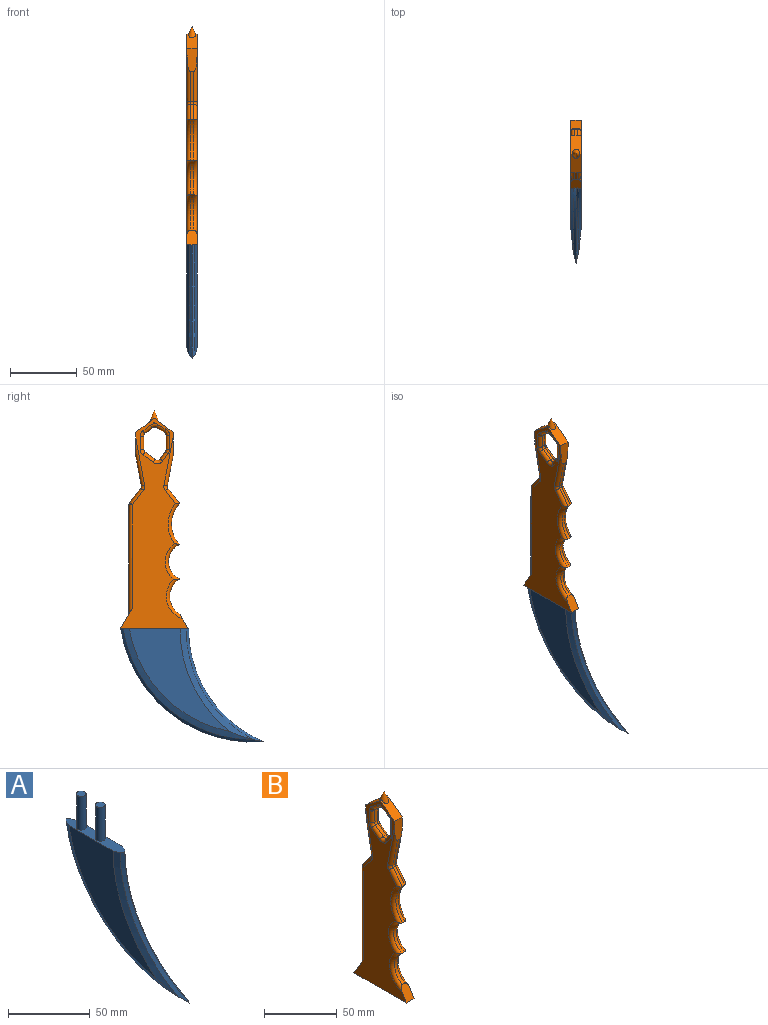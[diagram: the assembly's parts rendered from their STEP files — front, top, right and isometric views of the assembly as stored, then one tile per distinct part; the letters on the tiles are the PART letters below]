
ASSEMBLY  parts=2 mates=1
PART A: 15 faces, bbox 7.6x107.1x112.1 mm
  f0: plane 50.82x7.64mm, normal (0,0,1), area 295.1mm2, adj f1,f2,f3,f4,f5,f6,f7,f8
  f1: plane 76.85x75.17mm, normal (1,0,0), area 2128.3mm2, adj f0,f9,f10
  f2: plane 76.85x75.17mm, normal (-1,0,0), area 2128.3mm2, adj f0,f7,f8
  f3: cone r=100.59mm half-angle=45deg, axis (1,0,0), area 410.6mm2, adj f0,f4,f5,f7
  f4: cone r=96.78mm half-angle=45deg, axis (-1,0,0), area 410.6mm2, adj f0,f3,f6,f9
  f5: cone r=95.52mm half-angle=45deg, axis (-1,0,0), area 298.2mm2, adj f0,f3,f6,f8
  f6: cone r=91.71mm half-angle=45deg, axis (1,0,0), area 298.2mm2, adj f0,f4,f5,f10
  f7: cone r=94.24mm half-angle=67.5deg, axis (1,0,0), area 593mm2, adj f0,f2,f3,f8
  f8: cone r=98.06mm half-angle=67.5deg, axis (-1,0,0), area 446.1mm2, adj f0,f2,f5,f7
  f9: cone r=94.24mm half-angle=67.5deg, axis (-1,0,0), area 593mm2, adj f0,f1,f4,f10
  f10: cone r=98.06mm half-angle=67.5deg, axis (1,0,0), area 446.1mm2, adj f0,f1,f6,f9
  f11: cylinder r=2.92mm len=25.4mm, axis (0,0,-1), area 466.2mm2, adj f0,f12
  f12: plane 5.84x5.84mm, normal (0,0,1), area 26.8mm2, adj f11
  f13: cylinder r=2.92mm len=25.4mm, axis (0,0,-1), area 466.2mm2, adj f0,f14
  f14: plane 5.84x5.84mm, normal (0,0,1), area 26.8mm2, adj f13
PART B: 88 faces, bbox 7.7x50.9x163.9 mm
  f0: plane 157.82x50.89mm, normal (-1,0,0), area 3543.2mm2, adj f1,f2,f3,f55,f56,f57,f58,f59
  f1: cone r=0mm half-angle=21.7deg, axis (0,0,-1), area 0mm2, adj f0,f2
  f2: cone r=3.83mm half-angle=54.1deg, axis (0,0,-1), area 0mm2, adj f0,f1
  f3: cylinder r=2.54mm len=6.96mm, axis (0,0.6,-0.8), area 27.1mm2, adj f0,f4,f55,f65
  f4: plane 5.44x4.07mm, normal (0,0.8,0.6), area 17.3mm2, adj f3,f5,f53,f54
  f5: cylinder r=2.54mm len=2.54mm, axis (-1,0,0), area 4.1mm2, adj f4,f6,f52,f55
  f6: torus R=5.08mm, axis (1,0,0), area 8.9mm2, adj f5,f7,f25,f54
  f7: cylinder r=2.54mm len=10.95mm, axis (0,0,1), area 43.7mm2, adj f6,f8,f25,f52
  f8: torus R=5.08mm, axis (1,0,0), area 14.6mm2, adj f7,f9,f24,f25
  f9: cylinder r=2.54mm len=7.35mm, axis (0,0.87,0.49), area 28mm2, adj f8,f10,f23,f25
  f10: plane 6.11x3.45mm, normal (0,0.49,-0.87), area 17.8mm2, adj f9,f11,f24,f58
  f11: cylinder r=2.54mm len=2.8mm, axis (-1,0,0), area 7.6mm2, adj f10,f12,f23,f59
  f12: plane 5.62x4.33mm, normal (0,-0.61,-0.79), area 18mm2, adj f11,f13,f22,f60
  f13: cylinder r=2.54mm len=7.17mm, axis (0,0.79,-0.61), area 28.3mm2, adj f12,f14,f23,f25
  f14: torus R=5.08mm, axis (1,0,0), area 12.6mm2, adj f13,f15,f22,f25
  f15: cylinder r=2.54mm len=9.78mm, axis (0,0,-1), area 39mm2, adj f14,f16,f21,f25
  f16: plane 9.78x2.54mm, normal (0,-1,0), area 24.8mm2, adj f15,f17,f22,f62
  f17: cylinder r=2.54mm len=2.54mm, axis (-1,0,0), area 6mm2, adj f16,f18,f21,f63
  f18: plane 7.65x5.73mm, normal (0,-0.6,0.8), area 24.3mm2, adj f17,f19,f53,f64
  f19: cylinder r=2.54mm len=9.17mm, axis (0,-0.8,-0.6), area 38.1mm2, adj f18,f20,f21,f25
  f20: torus R=5.08mm, axis (1,0,0), area 21.7mm2, adj f19,f25,f53,f54
  f21: torus R=5.08mm, axis (1,0,0), area 12.8mm2, adj f15,f17,f19,f25
  f22: cylinder r=2.54mm len=2.54mm, axis (-1,0,0), area 5.9mm2, adj f12,f14,f16,f61
  f23: torus R=5.08mm, axis (1,0,0), area 16.2mm2, adj f9,f11,f13,f25
  f24: cylinder r=2.54mm len=2.54mm, axis (-1,0,0), area 6.8mm2, adj f8,f10,f52,f57
  f25: plane 157.82x50.89mm, normal (1,0,0), area 3543.2mm2, adj f6,f7,f8,f9,f13,f14,f15,f19
  f26: cone r=3.83mm half-angle=54.1deg, axis (0,0,-1), area 0mm2, adj f25,f27
  f27: cone r=0mm half-angle=21.7deg, axis (0,0,-1), area 0mm2, adj f25,f26
  f28: torus R=24.25mm, axis (1,0,0), area 132.7mm2, adj f25,f29,f35,f51
  f29: cylinder r=21.71mm len=30.54mm, axis (1,0,0), area 86mm2, adj f28,f30,f32,f84
  f30: cylinder r=13.99mm len=25.74mm, axis (1,0,0), area 83mm2, adj f29,f31,f51,f85
  f31: cylinder r=15.12mm len=26.27mm, axis (1,0,0), area 80.8mm2, adj f30,f50,f86,f87
  f32: plane 11.51x8.86mm, normal (0,-0.79,0.61), area 36.9mm2, adj f29,f33,f35,f83
  f33: cylinder r=2.54mm len=2.54mm, axis (1,0,0), area 5.5mm2, adj f32,f34,f36,f82
  f34: plane 22.53x4.34mm, normal (0,-0.98,-0.19), area 58.3mm2, adj f33,f37,f80,f81
  f35: cylinder r=2.54mm len=13.06mm, axis (0,-0.61,-0.79), area 54.8mm2, adj f25,f28,f32,f36
  f36: torus R=5.08mm, axis (1,0,0), area 11.7mm2, adj f25,f33,f35,f37
  f37: cylinder r=2.54mm len=35.96mm, axis (0,0.19,-0.98), area 110.7mm2, adj f25,f34,f36,f80
  f38: cylinder r=2.54mm len=35.68mm, axis (0,0.18,0.98), area 108.3mm2, adj f25,f39,f40,f47,f76
  f39: cylinder r=2.54mm len=3.47mm, axis (1,0,0), area 1.4mm2, adj f38,f40,f75,f76
  f40: plane 21.6x4.03mm, normal (0,0.98,-0.18), area 55.8mm2, adj f38,f39,f41,f75
  f41: cylinder r=2.54mm len=2.54mm, axis (-1,0,0), area 5.4mm2, adj f40,f42,f47,f74
  f42: plane 10.84x8.28mm, normal (0,0.79,0.61), area 34.6mm2, adj f41,f43,f48,f73
  f43: cylinder r=2.54mm len=2.54mm, axis (1,0,0), area 4.2mm2, adj f42,f44,f45,f46
  f44: sphere r=2.54mm, area 4.2mm2, adj f43,f72,f73
  f45: plane 81.69x2.54mm, normal (0,1,0), area 207.5mm2, adj f43,f49,f71,f72
  f46: sphere r=2.54mm, area 4.2mm2, adj f43,f48,f49
  f47: torus R=5.08mm, axis (1,0,0), area 11.6mm2, adj f25,f38,f41,f48
  f48: cylinder r=2.54mm len=12.38mm, axis (0,-0.61,0.79), area 54.4mm2, adj f25,f42,f46,f47
  f49: cylinder r=2.54mm len=81.69mm, axis (0,0,1), area 319.6mm2, adj f25,f45,f46,f71
  f50: torus R=17.66mm, axis (1,0,0), area 133.9mm2, adj f25,f31,f51,f87
  f51: torus R=16.53mm, axis (1,0,0), area 127.5mm2, adj f25,f28,f30,f50
  f52: plane 10.95x2.54mm, normal (0,1,0), area 27.8mm2, adj f5,f7,f24,f56
  f53: cylinder r=2.54mm len=3.56mm, axis (-1,0,0), area 10.1mm2, adj f4,f18,f20,f65
  f54: cylinder r=2.54mm len=6.96mm, axis (0,-0.6,0.8), area 27.1mm2, adj f4,f6,f20,f25
  f55: torus R=5.08mm, axis (1,0,0), area 8.9mm2, adj f0,f3,f5,f56
  f56: cylinder r=2.54mm len=10.95mm, axis (0,0,-1), area 43.7mm2, adj f0,f52,f55,f57
  f57: torus R=5.08mm, axis (1,0,0), area 14.6mm2, adj f0,f24,f56,f58
  f58: cylinder r=2.54mm len=7.35mm, axis (0,-0.87,-0.49), area 28mm2, adj f0,f10,f57,f59
  f59: torus R=5.08mm, axis (1,0,0), area 16.2mm2, adj f0,f11,f58,f60
  f60: cylinder r=2.54mm len=7.17mm, axis (0,-0.79,0.61), area 28.3mm2, adj f0,f12,f59,f61
  f61: torus R=5.08mm, axis (1,0,0), area 12.6mm2, adj f0,f22,f60,f62
  f62: cylinder r=2.54mm len=9.78mm, axis (0,0,1), area 39mm2, adj f0,f16,f61,f63
  f63: torus R=5.08mm, axis (1,0,0), area 12.8mm2, adj f0,f17,f62,f64
  f64: cylinder r=2.54mm len=9.17mm, axis (0,0.8,0.6), area 38.1mm2, adj f0,f18,f63,f65
  f65: torus R=5.08mm, axis (1,0,0), area 21.7mm2, adj f0,f3,f53,f64
  f66: plane 50.8x7.62mm, normal (0,0,-1), area 323.8mm2, adj f0,f25,f67,f69,f71,f87
  f67: cylinder r=3.17mm len=25.4mm, axis (0,0,-1), area 506.7mm2, adj f66,f68
  f68: cone r=0mm half-angle=59deg, axis (0,0,-1), area 36.9mm2, adj f67
  f69: cylinder r=3.17mm len=25.4mm, axis (0,0,-1), area 506.7mm2, adj f66,f70
  f70: cone r=0mm half-angle=59deg, axis (0,0,-1), area 36.9mm2, adj f69
  f71: plane 15.41x8.96mm, normal (0,0.86,0.5), area 102.8mm2, adj f0,f25,f45,f49,f66,f72
  f72: cylinder r=2.54mm len=81.69mm, axis (0,0,-1), area 319.6mm2, adj f0,f44,f45,f71
  f73: cylinder r=2.54mm len=12.38mm, axis (0,0.61,-0.79), area 54.4mm2, adj f0,f42,f44,f74
  f74: torus R=5.08mm, axis (1,0,0), area 11.6mm2, adj f0,f41,f73,f75
  f75: cylinder r=2.54mm len=35.68mm, axis (0,-0.18,-0.98), area 108.3mm2, adj f0,f39,f40,f74,f76
  f76: plane 17.95x7.62mm, normal (0,1,0), area 122.8mm2, adj f0,f25,f38,f39,f75,f77
  f77: plane 13.77x10.6mm, normal (0,0.61,0.79), area 113.7mm2, adj f0,f25,f76,f78,f79
  f78: cone r=0mm half-angle=21.7deg, axis (0,0,-1), area 79.4mm2, adj f77,f79
  f79: plane 14.12x10.57mm, normal (0,-0.6,0.8), area 116.2mm2, adj f0,f25,f77,f78,f80
  f80: plane 17.5x7.62mm, normal (0,-1,0), area 118.7mm2, adj f0,f25,f34,f37,f79,f81
  f81: cylinder r=2.54mm len=35.96mm, axis (0,-0.19,0.98), area 110.7mm2, adj f0,f34,f80,f82
  f82: torus R=5.08mm, axis (1,0,0), area 11.7mm2, adj f0,f33,f81,f83
  f83: cylinder r=2.54mm len=13.06mm, axis (0,0.61,0.79), area 54.8mm2, adj f0,f32,f82,f84
  f84: torus R=24.25mm, axis (1,0,0), area 132.7mm2, adj f0,f29,f83,f85
  f85: torus R=16.53mm, axis (1,0,0), area 127.5mm2, adj f0,f30,f84,f86
  f86: torus R=17.66mm, axis (1,0,0), area 133.9mm2, adj f0,f31,f85,f87
  f87: plane 11.04x7.62mm, normal (0,-0.87,0.49), area 91.8mm2, adj f0,f25,f31,f50,f66,f86
PLACE A t=(42.22,64.8,-143.19)mm
PLACE B t=(42.22,65.05,-264.1)mm
MATE fastened B.f69 <-> A.f11  axis (0,0,-1) through (42.22,77.12,-117.79)mm
